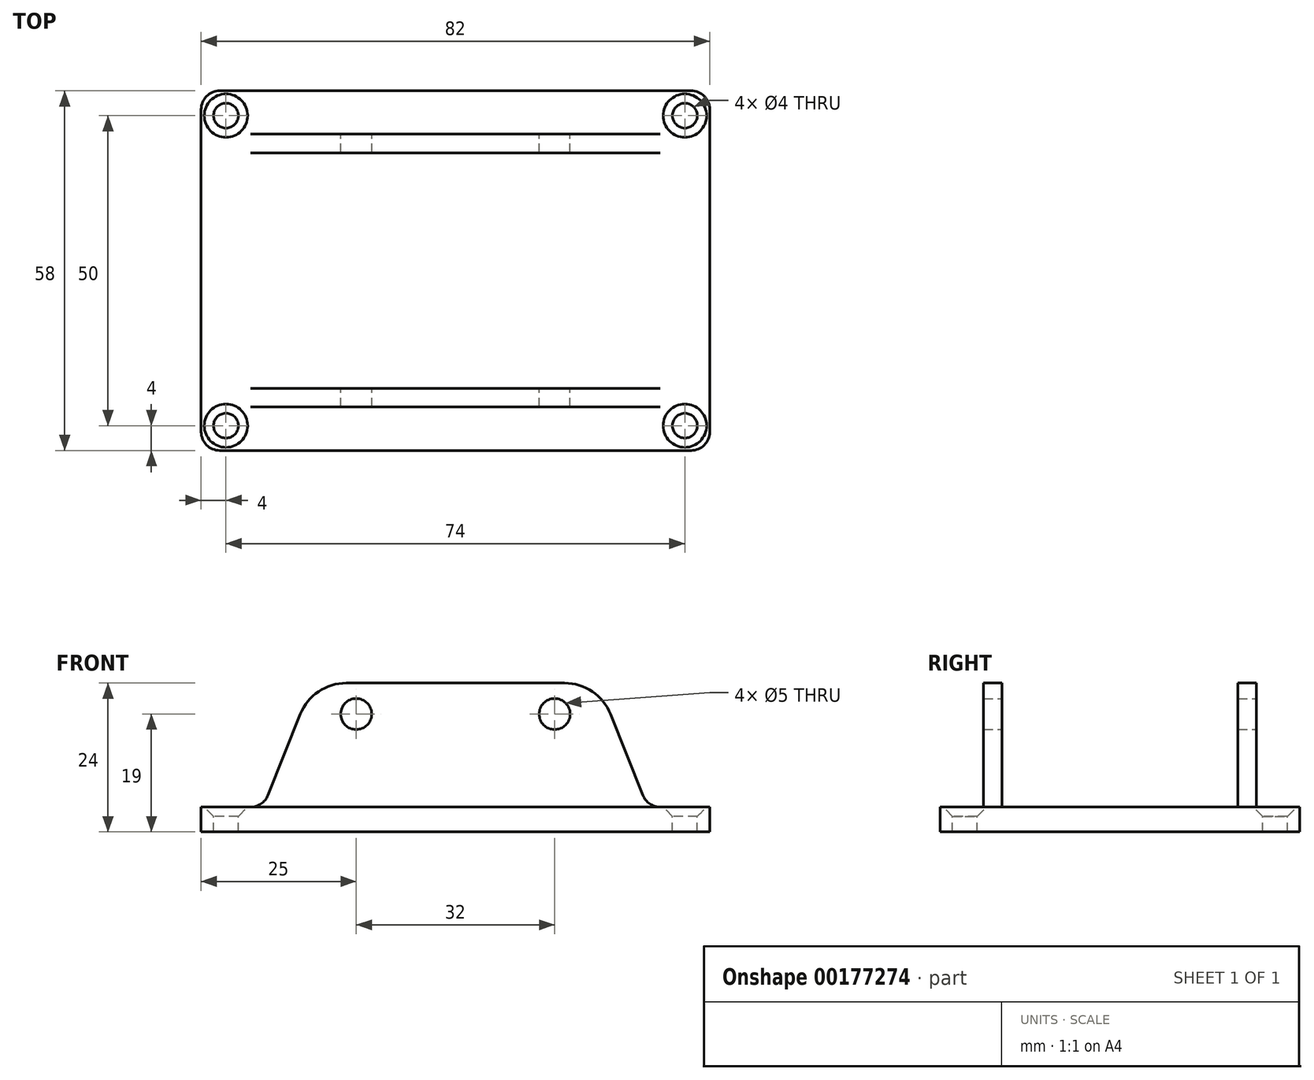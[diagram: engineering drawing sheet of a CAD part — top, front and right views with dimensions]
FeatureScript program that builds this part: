
annotation { "Feature Type Name" : "Feature", "Feature Type Description" : "" }
export const myFeature = defineFeature(function(context is Context, id is Id, definition is map)
    precondition{}
    {
        {
            var Q0;
            Q0=qCreatedBy(makeId("Top.planeOp"),FACE);
            var sketch = newSketch(context, id + "F0", { "sketchPlane" : qUnion([Q0])});
            skLineSegment(sketch, "E0.bottom", {"start": v(-62, 0) * mm, "end": v(0, 0) * mm, "construction": true});
            skLineSegment(sketch, "E0.top", {"start": v(-62, 38) * mm, "end": v(0, 38) * mm, "construction": true});
            skLineSegment(sketch, "E0.left", {"start": v(-62, 0) * mm, "end": v(-62, 38) * mm, "construction": true});
            skLineSegment(sketch, "E0.right", {"start": v(0, 0) * mm, "end": v(0, 38) * mm, "construction": true});
            skLineSegment(sketch, "E1", {"start": v(-15, 0) * mm, "end": v(-15, 38) * mm});
            skLineSegment(sketch, "E2", {"start": v(-47, 38) * mm, "end": v(-47, 0) * mm});
            skLineSegment(sketch, "E3.0", {"start": v(-72, -10) * mm, "end": v(10, -10) * mm});
            skLineSegment(sketch, "E3.1", {"start": v(-72, -10) * mm, "end": v(-72, 48) * mm});
            skLineSegment(sketch, "E3.2", {"start": v(-72, 48) * mm, "end": v(10, 48) * mm});
            skLineSegment(sketch, "E3.3", {"start": v(10, -10) * mm, "end": v(10, 48) * mm});
            skLineSegment(sketch, "E4.bottom", {"start": v(-62, 38) * mm, "end": v(0, 38) * mm});
            skLineSegment(sketch, "E4.top", {"start": v(-62, 41) * mm, "end": v(0, 41) * mm});
            skLineSegment(sketch, "E4.left", {"start": v(-62, 38) * mm, "end": v(-62, 41) * mm});
            skLineSegment(sketch, "E4.right", {"start": v(0, 38) * mm, "end": v(0, 41) * mm});
            skPoint(sketch, "E5.oppositeSnap0", {"position": v(0, 39.5) * mm});
            skLineSegment(sketch, "E5.bottom", {"start": v(-62, 0) * mm, "end": v(0, 0) * mm});
            skLineSegment(sketch, "E5.top", {"start": v(-62, -3) * mm, "end": v(0, -3) * mm});
            skLineSegment(sketch, "E5.left", {"start": v(-62, 0) * mm, "end": v(-62, -3) * mm});
            skLineSegment(sketch, "E5.right", {"start": v(0, 0) * mm, "end": v(0, -3) * mm});
            skCircle(sketch, "E6", {"center": v(6, -6) * mm, "radius": 2 * mm});
            skLineSegment(sketch, "E7", {"start": v(10, 19) * mm, "end": v(-72, 19) * mm, "construction": true});
            skLineSegment(sketch, "E8", {"start": v(-31, -10) * mm, "end": v(-31, 48) * mm, "construction": true});
            skCircle(sketch, "E9.MirrorC", {"center": v(6, 44) * mm, "radius": 2 * mm});
            skCircle(sketch, "E10.MirrorC", {"center": v(-68, -6) * mm, "radius": 2 * mm});
            skCircle(sketch, "E11.MirrorC", {"center": v(-68, 44) * mm, "radius": 2 * mm});
            skSolve(sketch);
        }
        {
            var Q0;
            Q0=makeQuery(id+"F0.imprint","IMPRINT",FACE,{"disambiguationData":[TD([[makeQuery(id+"F0.imprint","IMPRINT",EDGE,{"derivedFrom":sQuery(id+"F0.wireOp",EDGE,"E3.0")}),1.0]])]});
            var Q1;
            Q1=makeQuery(id+"F0.imprint","IMPRINT",FACE,{"disambiguationData":[TD([[makeQuery(id+"F0.imprint","IMPRINT",EDGE,{"derivedFrom":sQuery(id+"F0.wireOp",EDGE,"E5.bottom")}),-1.0]])]});
            var Q2;
            Q2=makeQuery(id+"F0.imprint","IMPRINT",FACE,{"disambiguationData":[TD([[makeQuery(id+"F0.imprint","IMPRINT",EDGE,{"derivedFrom":sQuery(id+"F0.wireOp",EDGE,"E4.bottom")}),1.0]])]});
            var Q3;
            {var subQ0=sQuery(id+"F0.wireOp",EDGE,"E1");Q3=makeQuery(id+"F0.imprint","IMPRINT",FACE,{"disambiguationData":[TD([[makeQuery(id+"F0.imprint","IMPRINT",EDGE,{"derivedFrom":subQ0}),1.0]])]});}
            extrude(context, id + "F1", {"entities" : qUnion([Q0, Q1, Q2, Q3]), "oppositeDirection" : true, "depth" : 4 * mm});
        }
        {
            var Q0;
            Q0=makeQuery(id+"F0.imprint","IMPRINT",FACE,{"disambiguationData":[TD([[makeQuery(id+"F0.imprint","IMPRINT",EDGE,{"derivedFrom":sQuery(id+"F0.wireOp",EDGE,"E4.bottom")}),1.0]])]});
            var Q1;
            Q1=makeQuery(id+"F0.imprint","IMPRINT",FACE,{"disambiguationData":[TD([[makeQuery(id+"F0.imprint","IMPRINT",EDGE,{"derivedFrom":sQuery(id+"F0.wireOp",EDGE,"E5.bottom")}),-1.0]])]});
            extrude(context, id + "F2", {"entities" : qUnion([Q0, Q1]), "operationType" : NewBodyOperationType.ADD, "depth" : 20 * mm});
        }
        {
            var Q0;
            Q0=makeQuery(id+"F2.opExtrude","SWEPT_FACE",FACE,{"disambiguationData":[OSD([sQuery(id+"F0.wireOp",EDGE,"E5.bottom")])]});
            var sketch = newSketch(context, id + "F3", { "sketchPlane" : qUnion([Q0])});
            skCircle(sketch, "E12", {"center": v(15, 15) * mm, "radius": 2.5 * mm});
            skCircle(sketch, "E13", {"center": v(47, 15) * mm, "radius": 2.5 * mm});
            skSolve(sketch);
        }
        {
            var Q0;
            Q0=makeQuery(id+"F3.imprint","IMPRINT",FACE,{"disambiguationData":[TD([[makeQuery(id+"F3.imprint","IMPRINT",EDGE,{"derivedFrom":sQuery(id+"F3.wireOp",EDGE,"E12")}),1.0]])]});
            var Q1;
            Q1=makeQuery(id+"F3.imprint","IMPRINT",FACE,{"disambiguationData":[TD([[makeQuery(id+"F3.imprint","IMPRINT",EDGE,{"derivedFrom":sQuery(id+"F3.wireOp",EDGE,"E13")}),1.0]])]});
            extrude(context, id + "F4", {"entities" : qUnion([Q0, Q1]), "operationType" : NewBodyOperationType.REMOVE, "endBound" : BoundingType.SYMMETRIC, "oppositeDirection" : true, "depth" : 100 * mm});
        }
        {
            var Q0;
            Q0=makeQuery(id+"F2.opExtrude","CAP_EDGE",EDGE,{"disambiguationData":[OSD([sQuery(id+"F0.wireOp",EDGE,"E5.right")])],"isStart":false});
            var Q1;
            Q1=makeQuery(id+"F2.opExtrude","CAP_EDGE",EDGE,{"disambiguationData":[OSD([sQuery(id+"F0.wireOp",EDGE,"E4.left")])],"isStart":false});
            var Q2;
            Q2=makeQuery(id+"F2.opExtrude","CAP_EDGE",EDGE,{"disambiguationData":[OSD([sQuery(id+"F0.wireOp",EDGE,"E5.left")])],"isStart":false});
            chamfer(context, id + "F5", {"entities" : qUnion([Q0, Q1, Q2]), "chamferType" : ChamferType.TWO_OFFSETS, "width1" : 20 * mm, "oppositeDirection" : false, "width2" : 8 * mm, "tangentPropagation" : true});
        }
        {
            var Q0;
            Q0=makeQuery(id+"F2.opExtrude","CAP_EDGE",EDGE,{"disambiguationData":[OSD([sQuery(id+"F0.wireOp",EDGE,"E4.right")])],"isStart":false});
            chamfer(context, id + "F6", {"entities" : qUnion([Q0]), "chamferType" : ChamferType.TWO_OFFSETS, "width1" : 20 * mm, "oppositeDirection" : true, "width2" : 8 * mm, "tangentPropagation" : true});
        }
        {
            var Q0;
            {var subQ0=sQuery(id+"F0.wireOp",EDGE,"E4.right");Q0=makeQuery(id+"F6.opChamfer","BLEND_EDGE",EDGE,{"blendedFrom":[makeQuery(id+"F2.opExtrude","CAP_EDGE",EDGE,{"disambiguationData":[OSD([subQ0])],"isStart":false}),makeQuery(id+"F2.opExtrude","CAP_FACE",FACE,{"disambiguationData":[OSD([sQuery(id+"F0.wireOp",EDGE,"E4.bottom"),sQuery(id+"F0.wireOp",EDGE,"E4.top"),sQuery(id+"F0.wireOp",EDGE,"E4.left"),subQ0])],"isStart":false})],"blendedInto":[makeQuery(id+"F2.opExtrude","CAP_FACE",FACE,{"disambiguationData":[OSD([sQuery(id+"F0.wireOp",EDGE,"E4.bottom"),sQuery(id+"F0.wireOp",EDGE,"E4.top"),sQuery(id+"F0.wireOp",EDGE,"E4.left"),subQ0])],"isStart":false})]});}
            var Q1;
            {var subQ0=sQuery(id+"F0.wireOp",EDGE,"E5.right");Q1=makeQuery(id+"F5.opChamfer","BLEND_EDGE",EDGE,{"blendedFrom":[makeQuery(id+"F2.opExtrude","CAP_EDGE",EDGE,{"disambiguationData":[OSD([subQ0])],"isStart":false}),makeQuery(id+"F2.opExtrude","CAP_FACE",FACE,{"disambiguationData":[OSD([sQuery(id+"F0.wireOp",EDGE,"E5.bottom"),sQuery(id+"F0.wireOp",EDGE,"E5.top"),sQuery(id+"F0.wireOp",EDGE,"E5.left"),subQ0])],"isStart":false})],"blendedInto":[makeQuery(id+"F2.opExtrude","CAP_FACE",FACE,{"disambiguationData":[OSD([sQuery(id+"F0.wireOp",EDGE,"E5.bottom"),sQuery(id+"F0.wireOp",EDGE,"E5.top"),sQuery(id+"F0.wireOp",EDGE,"E5.left"),subQ0])],"isStart":false})]});}
            var Q2;
            {var subQ0=sQuery(id+"F0.wireOp",EDGE,"E5.left");Q2=makeQuery(id+"F5.opChamfer","BLEND_EDGE",EDGE,{"blendedFrom":[makeQuery(id+"F2.opExtrude","CAP_EDGE",EDGE,{"disambiguationData":[OSD([subQ0])],"isStart":false}),makeQuery(id+"F2.opExtrude","CAP_FACE",FACE,{"disambiguationData":[OSD([sQuery(id+"F0.wireOp",EDGE,"E5.bottom"),sQuery(id+"F0.wireOp",EDGE,"E5.top"),subQ0,sQuery(id+"F0.wireOp",EDGE,"E5.right")])],"isStart":false})],"blendedInto":[makeQuery(id+"F2.opExtrude","CAP_FACE",FACE,{"disambiguationData":[OSD([sQuery(id+"F0.wireOp",EDGE,"E5.bottom"),sQuery(id+"F0.wireOp",EDGE,"E5.top"),subQ0,sQuery(id+"F0.wireOp",EDGE,"E5.right")])],"isStart":false})]});}
            var Q3;
            {var subQ0=sQuery(id+"F0.wireOp",EDGE,"E4.left");Q3=makeQuery(id+"F5.opChamfer","BLEND_EDGE",EDGE,{"blendedFrom":[makeQuery(id+"F2.opExtrude","CAP_EDGE",EDGE,{"disambiguationData":[OSD([subQ0])],"isStart":false}),makeQuery(id+"F2.opExtrude","CAP_FACE",FACE,{"disambiguationData":[OSD([sQuery(id+"F0.wireOp",EDGE,"E4.bottom"),sQuery(id+"F0.wireOp",EDGE,"E4.top"),subQ0,sQuery(id+"F0.wireOp",EDGE,"E4.right")])],"isStart":false})],"blendedInto":[makeQuery(id+"F2.opExtrude","CAP_FACE",FACE,{"disambiguationData":[OSD([sQuery(id+"F0.wireOp",EDGE,"E4.bottom"),sQuery(id+"F0.wireOp",EDGE,"E4.top"),subQ0,sQuery(id+"F0.wireOp",EDGE,"E4.right")])],"isStart":false})]});}
            fillet(context, id + "F7", {"entities" : qUnion([Q0, Q1, Q2, Q3]), "radius" : 8 * mm, "tangentPropagation" : true, "allowEdgeOverflow" : false});
        }
        {
            var Q0;
            Q0=makeQuery(id+"F2.opExtrude","CAP_EDGE",EDGE,{"disambiguationData":[OSD([sQuery(id+"F0.wireOp",EDGE,"E4.top")])],"isStart":true});
            var Q1;
            Q1=makeQuery(id+"F2.opExtrude","CAP_EDGE",EDGE,{"disambiguationData":[OSD([sQuery(id+"F0.wireOp",EDGE,"E4.bottom")])],"isStart":true});
            var Q2;
            Q2=makeQuery(id+"F2.opExtrude","CAP_EDGE",EDGE,{"disambiguationData":[OSD([sQuery(id+"F0.wireOp",EDGE,"E5.bottom")])],"isStart":true});
            var Q3;
            Q3=makeQuery(id+"F2.opExtrude","CAP_EDGE",EDGE,{"disambiguationData":[OSD([sQuery(id+"F0.wireOp",EDGE,"E5.top")])],"isStart":true});
            var Q4;
            Q4=makeQuery(id+"F5.opChamfer","BLEND_EDGE",EDGE,{"blendedFrom":[makeQuery(id+"F2.opExtrude","CAP_EDGE",EDGE,{"disambiguationData":[OSD([sQuery(id+"F0.wireOp",EDGE,"E5.right")])],"isStart":false}),makeQuery(id+"F1.opExtrude","CAP_FACE",FACE,{"disambiguationData":[OSD([sQuery(id+"F0.wireOp",EDGE,"E3.0"),sQuery(id+"F0.wireOp",EDGE,"E3.1"),sQuery(id+"F0.wireOp",EDGE,"E3.2"),sQuery(id+"F0.wireOp",EDGE,"E3.3")])],"isStart":true})],"blendedInto":[makeQuery(id+"F1.opExtrude","CAP_FACE",FACE,{"disambiguationData":[OSD([sQuery(id+"F0.wireOp",EDGE,"E3.0"),sQuery(id+"F0.wireOp",EDGE,"E3.1"),sQuery(id+"F0.wireOp",EDGE,"E3.2"),sQuery(id+"F0.wireOp",EDGE,"E3.3")])],"isStart":true})]});
            var Q5;
            Q5=makeQuery(id+"F6.opChamfer","BLEND_EDGE",EDGE,{"blendedFrom":[makeQuery(id+"F2.opExtrude","CAP_EDGE",EDGE,{"disambiguationData":[OSD([sQuery(id+"F0.wireOp",EDGE,"E4.right")])],"isStart":false}),makeQuery(id+"F1.opExtrude","CAP_FACE",FACE,{"disambiguationData":[OSD([sQuery(id+"F0.wireOp",EDGE,"E3.0"),sQuery(id+"F0.wireOp",EDGE,"E3.1"),sQuery(id+"F0.wireOp",EDGE,"E3.2"),sQuery(id+"F0.wireOp",EDGE,"E3.3")])],"isStart":true})],"blendedInto":[makeQuery(id+"F1.opExtrude","CAP_FACE",FACE,{"disambiguationData":[OSD([sQuery(id+"F0.wireOp",EDGE,"E3.0"),sQuery(id+"F0.wireOp",EDGE,"E3.1"),sQuery(id+"F0.wireOp",EDGE,"E3.2"),sQuery(id+"F0.wireOp",EDGE,"E3.3")])],"isStart":true})]});
            var Q6;
            Q6=makeQuery(id+"F5.opChamfer","BLEND_EDGE",EDGE,{"blendedFrom":[makeQuery(id+"F2.opExtrude","CAP_EDGE",EDGE,{"disambiguationData":[OSD([sQuery(id+"F0.wireOp",EDGE,"E5.left")])],"isStart":false}),makeQuery(id+"F1.opExtrude","CAP_FACE",FACE,{"disambiguationData":[OSD([sQuery(id+"F0.wireOp",EDGE,"E3.0"),sQuery(id+"F0.wireOp",EDGE,"E3.1"),sQuery(id+"F0.wireOp",EDGE,"E3.2"),sQuery(id+"F0.wireOp",EDGE,"E3.3")])],"isStart":true})],"blendedInto":[makeQuery(id+"F1.opExtrude","CAP_FACE",FACE,{"disambiguationData":[OSD([sQuery(id+"F0.wireOp",EDGE,"E3.0"),sQuery(id+"F0.wireOp",EDGE,"E3.1"),sQuery(id+"F0.wireOp",EDGE,"E3.2"),sQuery(id+"F0.wireOp",EDGE,"E3.3")])],"isStart":true})]});
            var Q7;
            Q7=makeQuery(id+"F5.opChamfer","BLEND_EDGE",EDGE,{"blendedFrom":[makeQuery(id+"F2.opExtrude","CAP_EDGE",EDGE,{"disambiguationData":[OSD([sQuery(id+"F0.wireOp",EDGE,"E4.left")])],"isStart":false}),makeQuery(id+"F1.opExtrude","CAP_FACE",FACE,{"disambiguationData":[OSD([sQuery(id+"F0.wireOp",EDGE,"E3.0"),sQuery(id+"F0.wireOp",EDGE,"E3.1"),sQuery(id+"F0.wireOp",EDGE,"E3.2"),sQuery(id+"F0.wireOp",EDGE,"E3.3")])],"isStart":true})],"blendedInto":[makeQuery(id+"F1.opExtrude","CAP_FACE",FACE,{"disambiguationData":[OSD([sQuery(id+"F0.wireOp",EDGE,"E3.0"),sQuery(id+"F0.wireOp",EDGE,"E3.1"),sQuery(id+"F0.wireOp",EDGE,"E3.2"),sQuery(id+"F0.wireOp",EDGE,"E3.3")])],"isStart":true})]});
            fillet(context, id + "F8", {"entities" : qUnion([Q0, Q1, Q2, Q3, Q4, Q5, Q6, Q7]), "radius" : 3 * mm, "tangentPropagation" : true, "allowEdgeOverflow" : false});
        }
        {
            var Q0;
            Q0=makeQuery(id+"F1.opExtrude","CAP_EDGE",EDGE,{"disambiguationData":[OSD([sQuery(id+"F0.wireOp",EDGE,"E6")])],"isStart":true});
            var Q1;
            Q1=makeQuery(id+"F1.opExtrude","CAP_EDGE",EDGE,{"disambiguationData":[OSD([sQuery(id+"F0.wireOp",EDGE,"E9.MirrorC")])],"isStart":true});
            var Q2;
            Q2=makeQuery(id+"F1.opExtrude","CAP_EDGE",EDGE,{"disambiguationData":[OSD([sQuery(id+"F0.wireOp",EDGE,"E11.MirrorC")])],"isStart":true});
            var Q3;
            Q3=makeQuery(id+"F1.opExtrude","CAP_EDGE",EDGE,{"disambiguationData":[OSD([sQuery(id+"F0.wireOp",EDGE,"E10.MirrorC")])],"isStart":true});
            chamfer(context, id + "F9", {"entities" : qUnion([Q0, Q1, Q2, Q3]), "width" : 1.5 * mm, "tangentPropagation" : true});
        }
        {
            var Q0;
            Q0=makeQuery(id+"F1.opExtrude","SWEPT_EDGE",EDGE,{"disambiguationData":[OSD([sQuery(id+"F0.wireOp",EDGE,"E3.0"),sQuery(id+"F0.wireOp",EDGE,"E3.3")])]});
            var Q1;
            Q1=makeQuery(id+"F1.opExtrude","SWEPT_EDGE",EDGE,{"disambiguationData":[OSD([sQuery(id+"F0.wireOp",EDGE,"E3.2"),sQuery(id+"F0.wireOp",EDGE,"E3.3")])]});
            var Q2;
            Q2=makeQuery(id+"F1.opExtrude","SWEPT_EDGE",EDGE,{"disambiguationData":[OSD([sQuery(id+"F0.wireOp",EDGE,"E3.0"),sQuery(id+"F0.wireOp",EDGE,"E3.1")])]});
            var Q3;
            Q3=makeQuery(id+"F1.opExtrude","SWEPT_EDGE",EDGE,{"disambiguationData":[OSD([sQuery(id+"F0.wireOp",EDGE,"E3.1"),sQuery(id+"F0.wireOp",EDGE,"E3.2")])]});
            fillet(context, id + "F10", {"entities" : qUnion([Q0, Q1, Q2, Q3]), "radius" : 3 * mm, "tangentPropagation" : true, "allowEdgeOverflow" : false});
        }
    });
